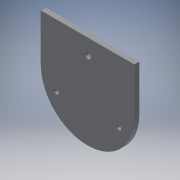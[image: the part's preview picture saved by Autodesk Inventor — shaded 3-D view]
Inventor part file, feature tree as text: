
AUTODESK INVENTOR PART (.ipt)
format: ipt  version: 2016 (Build 200138000, 138)  size: 145,920 bytes
history: native  units: in
note: dims shown in document units (in); Inventor stores cm internally (conversion verified against a paired STEP export)
features: reference x5, extrude x3, sketch x3, plane x1, projected_geometry x1
ambient origin geometry x8: Origin, YZ Plane, XZ Plane, XY Plane, X Axis, Y Axis, Z Axis, Center Point
bodies: Solid1 (feature_tree)
feature tree (13):
  extrude  "Extrusion1"  Depth=3.0in
  plane  "Work Plane1"
  extrude  "Extrusion2"  Depth=0.1575in
  extrude  "Extrusion3"  Depth=0.1575in
  sketch  "Sketch1"  dims[d0=1.0in d1=3.0in]
  reference  "Reference1"
  reference  "Reference2"
  sketch  "Sketch2"  dims[d2=0.1575in d3=0.0in d4=0.1969in]
  reference  "Reference3"
  sketch  "Sketch3"  dims[d5=0.1575in d6=0.0in d7=1.0in d8=2.0in d9=0.1575in d10=0.1575in d11=1.0in d12=0.0in]
  reference  "Reference4"
  reference  "Reference5"
  projected_geometry  "Projected Loop1"
